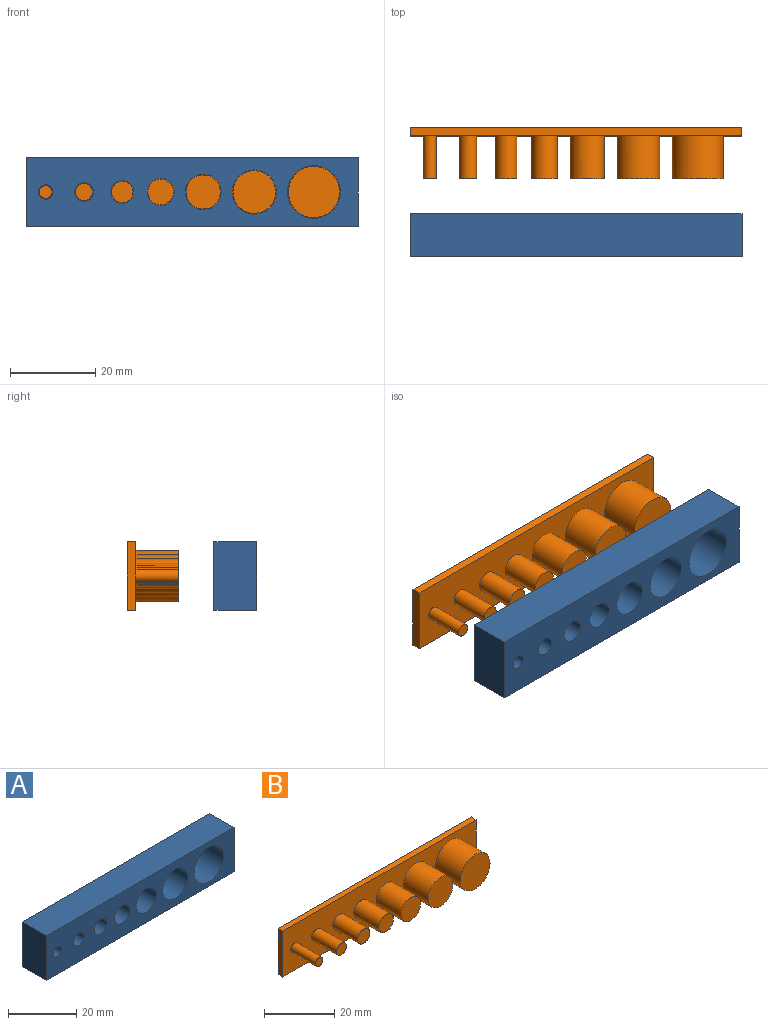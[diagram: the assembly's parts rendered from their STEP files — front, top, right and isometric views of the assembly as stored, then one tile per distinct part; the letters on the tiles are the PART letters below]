
ASSEMBLY  parts=2 mates=1
PART A: 13 faces, bbox 78x10x16 mm
  f0: plane 78x10mm, normal (0,0,1), area 780mm2, adj f1,f10,f11,f12
  f1: plane 16x10mm, normal (-1,0,0), area 160mm2, adj f0,f2,f11,f12
  f2: plane 78x10mm, normal (0,0,-1), area 780mm2, adj f1,f10,f11,f12
  f3: cylinder r=1.7mm len=10mm, axis (0,1,0), area 106.8mm2, adj f11,f12
  f4: cylinder r=2.2mm len=10mm, axis (0,1,0), area 138.2mm2, adj f11,f12
  f5: cylinder r=2.7mm len=10mm, axis (0,1,0), area 169.6mm2, adj f11,f12
  f6: cylinder r=3.2mm len=10mm, axis (0,1,0), area 201.1mm2, adj f11,f12
  f7: cylinder r=4.2mm len=10mm, axis (0,1,0), area 263.9mm2, adj f11,f12
  f8: cylinder r=5.2mm len=10.4mm, axis (0,1,0), area 326.7mm2, adj f11,f12
  f9: cylinder r=6.2mm len=12.4mm, axis (0,1,0), area 389.6mm2, adj f11,f12
  f10: plane 16x10mm, normal (1,0,0), area 160mm2, adj f0,f2,f11,f12
  f11: plane 78x16mm, normal (0,-1,0), area 907.5mm2, adj f0,f1,f2,f3,f4,f5,f6,f7
  f12: plane 78x16mm, normal (0,1,0), area 907.5mm2, adj f0,f1,f2,f3,f4,f5,f6,f7
PART B: 20 faces, bbox 78x12x16 mm
  f0: plane 78x2mm, normal (0,0,1), area 156mm2, adj f1,f3,f4,f5
  f1: plane 16x2mm, normal (-1,0,0), area 32mm2, adj f0,f2,f4,f5
  f2: plane 78x2mm, normal (0,0,-1), area 156mm2, adj f1,f3,f4,f5
  f3: plane 16x2mm, normal (1,0,0), area 32mm2, adj f0,f2,f4,f5
  f4: plane 78x16mm, normal (0,-1,0), area 938.6mm2, adj f0,f1,f2,f3,f6,f8,f10,f12
  f5: plane 78x16mm, normal (0,1,0), area 1248mm2, adj f0,f1,f2,f3
  f6: cylinder r=1.5mm len=10mm, axis (0,1,0), area 94.2mm2, adj f4,f7
  f7: plane 3x3mm, normal (0,-1,0), area 7.1mm2, adj f6
  f8: cylinder r=2mm len=10mm, axis (0,1,0), area 125.7mm2, adj f4,f9
  f9: plane 4x4mm, normal (0,-1,0), area 12.6mm2, adj f8
  f10: cylinder r=2.5mm len=10mm, axis (0,1,0), area 157.1mm2, adj f4,f11
  f11: plane 5x5mm, normal (0,-1,0), area 19.6mm2, adj f10
  f12: cylinder r=3mm len=10mm, axis (0,1,0), area 188.5mm2, adj f4,f13
  f13: plane 6x6mm, normal (0,-1,0), area 28.3mm2, adj f12
  f14: cylinder r=4mm len=10mm, axis (0,1,0), area 251.3mm2, adj f4,f15
  f15: plane 8x8mm, normal (0,-1,0), area 50.3mm2, adj f14
  f16: cylinder r=5mm len=10mm, axis (0,1,0), area 314.2mm2, adj f4,f17
  f17: plane 10x10mm, normal (0,-1,0), area 78.5mm2, adj f16
  f18: cylinder r=6mm len=12mm, axis (0,1,0), area 377mm2, adj f4,f19
  f19: plane 12x12mm, normal (0,-1,0), area 113.1mm2, adj f18
PLACE A t=(-7.82,-13.32,-6.07)mm
PLACE B t=(-7.99,7,-27.82)mm
MATE slider B.f18 <-> A.f9  axis (0,-1,0) through (23.04,-5,-27.82)mm
